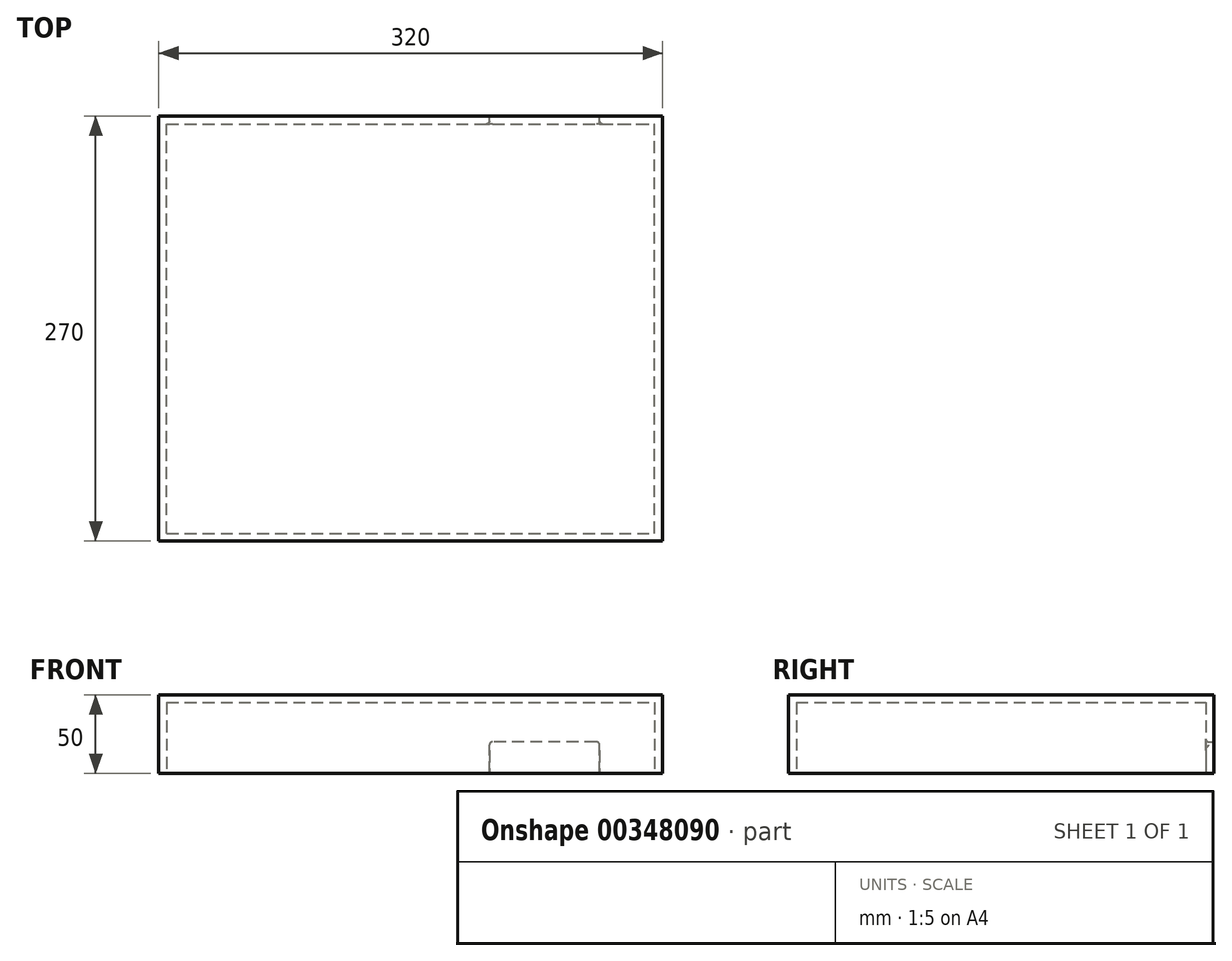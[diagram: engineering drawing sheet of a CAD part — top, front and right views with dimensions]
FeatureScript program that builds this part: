
annotation { "Feature Type Name" : "Feature", "Feature Type Description" : "" }
export const myFeature = defineFeature(function(context is Context, id is Id, definition is map)
    precondition{}
    {
        {
            var Q0;
            Q0=qCreatedBy(makeId("Front.planeOp"),FACE);
            var sketch = newSketch(context, id + "F0", { "sketchPlane" : qUnion([Q0])});
            skLineSegment(sketch, "E0.bottom", {"start": v(-196.4, 71.13) * mm, "end": v(123.6, 71.13) * mm});
            skLineSegment(sketch, "E0.top", {"start": v(-196.4, 21.13) * mm, "end": v(123.6, 21.13) * mm});
            skLineSegment(sketch, "E0.left", {"start": v(-196.4, 71.13) * mm, "end": v(-196.4, 21.13) * mm});
            skLineSegment(sketch, "E0.right", {"start": v(123.6, 71.13) * mm, "end": v(123.6, 21.13) * mm});
            skSolve(sketch);
        }
        {
            var Q0;
            Q0=makeQuery(id+"F0.imprint","IMPRINT",FACE,{"disambiguationData":[TD([[makeQuery(id+"F0.imprint","IMPRINT",EDGE,{"derivedFrom":sQuery(id+"F0.wireOp",EDGE,"E0.bottom")}),-1.0]])]});
            extrude(context, id + "F1", {"entities" : qUnion([Q0]), "depth" : 270 * mm});
        }
        {
            var Q0;
            Q0=makeQuery(id+"F1.opExtrude","SWEPT_FACE",FACE,{"disambiguationData":[OSD([sQuery(id+"F0.wireOp",EDGE,"E0.top")])]});
            shell(context, id + "F2", {"entities" : qUnion([Q0]), "thickness" : 5 * mm});
        }
        {
            var Q0;
            Q0=makeQuery(id+"F1.opExtrude","CAP_FACE",FACE,{"disambiguationData":[OSD([sQuery(id+"F0.wireOp",EDGE,"E0.bottom"),sQuery(id+"F0.wireOp",EDGE,"E0.top"),sQuery(id+"F0.wireOp",EDGE,"E0.left"),sQuery(id+"F0.wireOp",EDGE,"E0.right")])],"isStart":true});
            var sketch = newSketch(context, id + "F3", { "sketchPlane" : qUnion([Q0])});
            skLineSegment(sketch, "E1.bottom", {"start": v(-83.6, 21.13) * mm, "end": v(-13.6, 21.13) * mm});
            skLineSegment(sketch, "E1.top", {"start": v(-83.6, 41.13) * mm, "end": v(-13.6, 41.13) * mm});
            skLineSegment(sketch, "E1.left", {"start": v(-83.6, 21.13) * mm, "end": v(-83.6, 41.13) * mm});
            skLineSegment(sketch, "E1.right", {"start": v(-13.6, 21.13) * mm, "end": v(-13.6, 41.13) * mm});
            skLineSegment(sketch, "E2", {"start": v(-83.6, 41.13) * mm, "end": v(-123.6, 41.13) * mm});
            skSolve(sketch);
        }
        {
            var Q0;
            Q0=makeQuery(id+"F3.imprint","IMPRINT",FACE,{"disambiguationData":[TD([[makeQuery(id+"F3.imprint","IMPRINT",EDGE,{"derivedFrom":sQuery(id+"F3.wireOp",EDGE,"E1.bottom")}),-1.0]])]});
            extrude(context, id + "F4", {"entities" : qUnion([Q0]), "operationType" : NewBodyOperationType.REMOVE, "oppositeDirection" : true, "depth" : 25 * mm});
        }
        {
            var Q0;
            Q0=makeQuery(id+"F4.boolean.opBoolean","COPY",EDGE,{"derivedFrom":makeQuery(id+"F4.opExtrude","SWEPT_EDGE",EDGE,{"disambiguationData":[OSD([sQuery(id+"F0.wireOp",EDGE,"E0.top"),sQuery(id+"F3.wireOp",EDGE,"E1.bottom"),sQuery(id+"F3.wireOp",EDGE,"E1.left")])]})});
            var Q1;
            Q1=makeQuery(id+"F4.boolean.opBoolean","COPY",EDGE,{"derivedFrom":makeQuery(id+"F4.opExtrude","SWEPT_EDGE",EDGE,{"disambiguationData":[OSD([sQuery(id+"F3.wireOp",EDGE,"E1.top"),sQuery(id+"F3.wireOp",EDGE,"E1.left"),sQuery(id+"F3.wireOp",EDGE,"E2")])]})});
            var Q2;
            Q2=makeQuery(id+"F4.boolean.opBoolean","COPY",EDGE,{"derivedFrom":makeQuery(id+"F4.opExtrude","SWEPT_EDGE",EDGE,{"disambiguationData":[OSD([sQuery(id+"F3.wireOp",EDGE,"E1.top"),sQuery(id+"F3.wireOp",EDGE,"E1.right")])]})});
            var Q3;
            Q3=makeQuery(id+"F4.boolean.opBoolean","COPY",EDGE,{"derivedFrom":makeQuery(id+"F4.opExtrude","SWEPT_EDGE",EDGE,{"disambiguationData":[OSD([sQuery(id+"F0.wireOp",EDGE,"E0.top"),sQuery(id+"F3.wireOp",EDGE,"E1.bottom"),sQuery(id+"F3.wireOp",EDGE,"E1.right")])]})});
            var Q4;
            Q4=makeQuery(id+"F4.boolean.opBoolean","COPY",EDGE,{"derivedFrom":makeQuery(id+"F4.opExtrude","CAP_EDGE",EDGE,{"disambiguationData":[OSD([sQuery(id+"F3.wireOp",EDGE,"E1.top")])],"isStart":true})});
            var Q5;
            {var subQ0=sQuery(id+"F0.wireOp",EDGE,"E0.right");var subQ1=sQuery(id+"F0.wireOp",EDGE,"E0.left");var subQ2=sQuery(id+"F0.wireOp",EDGE,"E0.top");var subQ3=sQuery(id+"F0.wireOp",EDGE,"E0.bottom");Q5=makeQuery(id+"F4.boolean.opBoolean","INTERSECT",EDGE,{"derivedFrom":[makeQuery(id+"F2.opShell","OFFSET_FACE",FACE,{"disambiguationData":[OSD([subQ3,subQ2,subQ1,subQ0]),TDD([makeQuery(id+"F1.opExtrude","CAP_FACE",FACE,{"disambiguationData":[OSD([subQ3,subQ2,subQ1,subQ0])],"isStart":true})])]}),makeQuery(id+"F4.opExtrude","SWEPT_FACE",FACE,{"disambiguationData":[OSD([sQuery(id+"F3.wireOp",EDGE,"E1.top")])]})]});}
            fillet(context, id + "F5", {"entities" : qUnion([Q0, Q1, Q2, Q3, Q4, Q5]), "radius" : 2 * mm, "tangentPropagation" : true, "allowEdgeOverflow" : false});
        }
    });
